# Revit family: MTP cassettes
name_source: partatom
category: Installations électriques
units: mm (PartAtom-declared; Revit-internal decimal feet)

## family parameters
Basée sur le plan de construction = Non
Conserver l'orientation des annotations = Non
Cote de connecteur circulaire = Utiliser le diamètre
Couper avec des vides une fois chargée = Non
Partagée = Non
Point de calcul de pièce = Non
Toujours verticalement = Oui
Type d'élément = Normal

## types (8) — shared parameters
Color = IDS_NOIR
E-catalogue link = https://www.legrand.fr
Height = 43.7 mm  [stored 0.143373 ft]
Operating temperature = -10°C à 60°C
Storage temperature = -10°C à 60°C
Width (mm) = 110 mm  [stored 0.360892 ft]
With front plate = Non
With housing = Oui
With pigtails = Non
zero-valued in all types: Elévation par défaut

## per-type parameters (varying)
| type | Connectors visibility | Crossed | Depth | EAN | ETIM class | Fiber optic class | Fiber optic type | Function | LC connectors | LC connectors visibility | Legrand part number | Number of connectors front side | Number of connectors rear side | SC connectors | SC connectors visibility | Suitable for number of connectors | Type of connector external | Type of connector interior |
| MTP cassette 24 LC OM4 MTP HD panel Ultra | Oui | Non | 196 mm  [stored 0.643045 ft] | 3414970962140 | EC001130 | OM4 | Multimode | Slim cassettes High Density MTP | LC connectors : 24 fibers OM4 multi mode | Oui | 032142 | 24 | 2 | SC connectors : 12 fibers OM4 multi mode | Non | 24 | LC_DUPLEX | MT/MPO |
| MTP cassette 12 SC OM4 HD panel Ultra | Non | Oui | 196 mm  [stored 0.643045 ft] | 3414970962164 | EC001130 | OM4 | Multimode | Slim cassettes High Density MTP | LC connectors : 12 fibers OM4 multi mode | Non | 032143 | 12 | 1 | SC connectors : 12 fibers OM4 multi mode | Oui | 12 | SC_DUPLEX | MT/MPO |
| MTP cassette 24 LC OS2 MTP HD panel Ultra | Oui | Non | 196 mm  [stored 0.643045 ft] | 3414970962188 | EC001130 | OS2 | Single mode | Slim cassettes High Density MTP | LC connectors : 24 fibers OS2 single mode | Oui | 032144 | 24 | 2 | SC connectors : 12 fibers OM4 multi mode | Non | 24 | LC_DUPLEX | MT/MPO |
| MTP cassette 12 SC OS2 MTP HD panel Ultra | Non | Oui | 196 mm  [stored 0.643045 ft] | 3414970962201 | EC001130 | OS2 | Single mode | Slim cassettes High Density MTP | LC connectors : 12 fibers OM4 multi mode | Non | 032145 | 12 | 1 | SC connectors : 12 fibers OS2 single mode | Oui | 12 | SC_DUPLEX | MT/MPO |
| MTP cassette 12 LC OM4 MTP HD panel Ultra | Non | Non | 200 mm  [stored 0.656168 ft] | 3414971420236 | EC002699 | OM4 | Multimode | High density MTP cassettes | LC connectors : 12 fibers OM4 multi mode | Oui | 032148 | 12 | 1 | SC connectors : 12 fibers OM4 multi mode | Non | 12 | LC_DUPLEX | MTP-M |
| MTP cassette 12 LC OS2 MTP HD panel Ultra | Non | Non | 200 mm  [stored 0.656168 ft] | 3414971420250 | EC002699 | OS2 | Single mode | High density MTP cassettes | LC connectors : 12 fibers OS2 single mode | Oui | 032149 | 12 | 1 | SC connectors : 12 fibers OM4 multi mode | Non | 12 | LC_DUPLEX | MTP-M |
| MTP cassette 12 SC OM4 MTP HD panelÉ_UNIVERSELLE_ULTRA | Non | Oui | 200 mm  [stored 0.656168 ft] | 3414971929296 | EC002699 | OM4 | Multimode | High density MTP cassettes | LC connectors : 12 fibers OM4 multi mode | Non | 032159 | 12 | 1 | SC connectors : 12 fibers OM4 multi mode | Oui | 12 | SC_DUPLEX | MTP-M |
| MTP cassette 12 SC OS2 universal polarity Ultra | Non | Oui | 200 mm  [stored 0.656168 ft] | 3414971929319 | EC002699 | OS2 | Single mode | High density MTP cassettes | LC connectors : 12 fibers OM4 multi mode | Non | 032160 | 12 | 1 | SC connectors : 12 fibers OS2 single mode | Oui | 12 | SC_DUPLEX | MTP-M |

note: column(s) folded — value = type name in every type: BIM wording

note: [stored X ft] marks values corroborated as IEEE doubles in the binary element streams (Revit-internal decimal feet)
